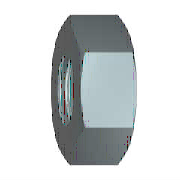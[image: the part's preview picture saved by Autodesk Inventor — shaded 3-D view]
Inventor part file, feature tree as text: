
AUTODESK INVENTOR PART (.ipt)
format: ipt  version: 2023 (Build 270158000, 158)  size: 164,864 bytes
history: native  units: mm (DEFAULTED — no unit token found)
features: sketch x3, other x2, extrude x1, hole x1, plane x1
ambient origin geometry x7: Origin, YZ Plane, XZ Plane, X Axis, Y Axis, Z Axis, Center Point
bodies: Solid1 (feature_tree)
feature tree (8):
  extrude  "Базовый элемент"  Depth=15.011107mm
  other  "Фаска1"
  hole  "Резьба"  [1 undecoded]
  other  "Work Axis1"
  plane  "Work Plane1"
  sketch  "Эскиз1"
  sketch  "Эскиз2"
  sketch  "Эскиз3"
note: 1 required parameter value undecoded (feature->parameter linkage not recoverable at this tier; creation-order binding heuristic only, values carry confidence <= 0.55)
